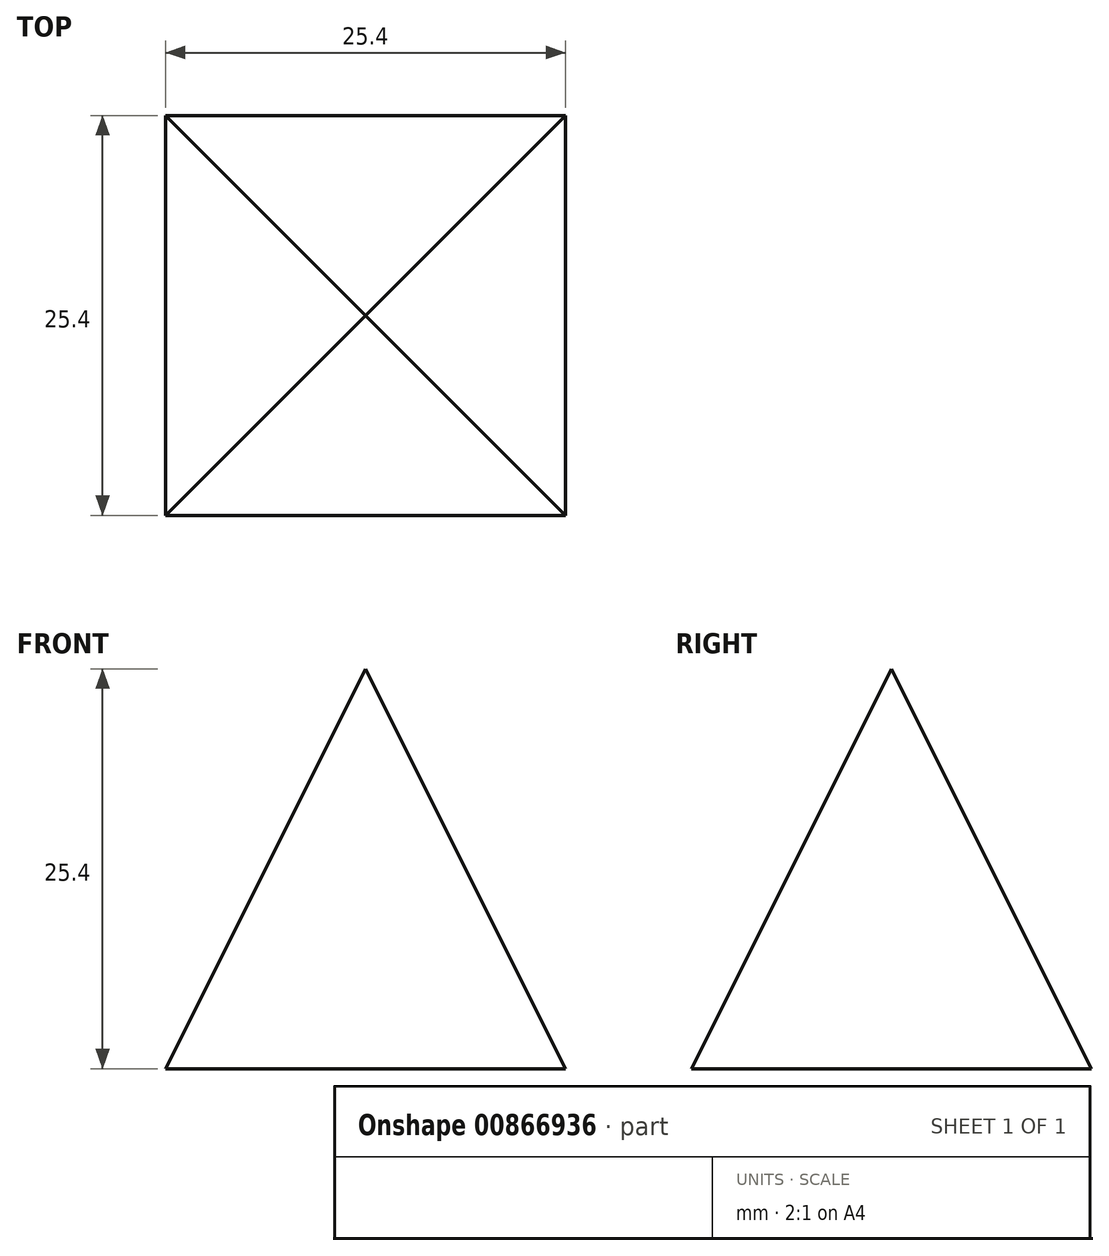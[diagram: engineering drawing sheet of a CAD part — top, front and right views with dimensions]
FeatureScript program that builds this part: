
annotation { "Feature Type Name" : "Feature", "Feature Type Description" : "" }
export const myFeature = defineFeature(function(context is Context, id is Id, definition is map)
    precondition{}
    {
        {
            var Q0;
            Q0=qCreatedBy(makeId("Front.planeOp"),FACE);
            var sketch = newSketch(context, id + "F0", { "sketchPlane" : qUnion([Q0])});
            skLineSegment(sketch, "E0.bottom", {"start": v(0, 0) * mm, "end": v(25.4, 0) * mm});
            skLineSegment(sketch, "E0.top", {"start": v(0, 25.4) * mm, "end": v(25.4, 25.4) * mm});
            skLineSegment(sketch, "E0.left", {"start": v(0, 0) * mm, "end": v(0, 25.4) * mm});
            skLineSegment(sketch, "E0.right", {"start": v(25.4, 0) * mm, "end": v(25.4, 25.4) * mm});
            skSolve(sketch);
        }
        {
            var Q0;
            Q0=makeQuery(id+"F0.imprint","IMPRINT",FACE,{"disambiguationData":[TD([[makeQuery(id+"F0.imprint","IMPRINT",EDGE,{"derivedFrom":sQuery(id+"F0.wireOp",EDGE,"E0.bottom")}),1.0]])]});
            extrude(context, id + "F1", {"entities" : qUnion([Q0]), "depth" : 25.4 * mm, "offsetDistance" : 25.4 * mm});
        }
        {
            var Q0;
            Q0=makeQuery(id+"F1.opExtrude","SWEPT_FACE",FACE,{"disambiguationData":[OSD([sQuery(id+"F0.wireOp",EDGE,"E0.top")])]});
            chamfer(context, id + "F2", {"entities" : qUnion([Q0]), "chamferType" : ChamferType.TWO_OFFSETS, "width1" : 25.4 * mm, "oppositeDirection" : false, "width2" : 12.7 * mm, "tangentPropagation" : true});
        }
    });
